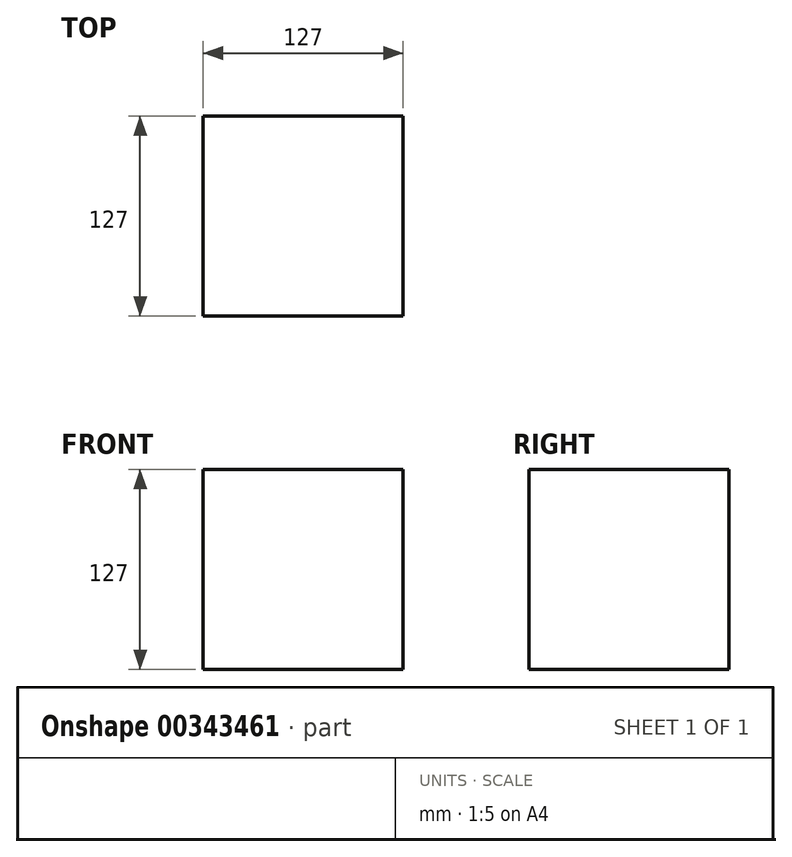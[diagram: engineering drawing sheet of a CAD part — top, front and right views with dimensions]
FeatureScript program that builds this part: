
annotation { "Feature Type Name" : "Feature", "Feature Type Description" : "" }
export const myFeature = defineFeature(function(context is Context, id is Id, definition is map)
    precondition{}
    {
        {
            var Q0;
            Q0=qCreatedBy(makeId("Front.planeOp"),FACE);
            var sketch = newSketch(context, id + "F0", { "sketchPlane" : qUnion([Q0])});
            skLineSegment(sketch, "E0.bottom", {"start": v(-90.88, 157.92) * mm, "end": v(36.12, 157.92) * mm});
            skLineSegment(sketch, "E0.top", {"start": v(-90.88, 30.92) * mm, "end": v(36.12, 30.92) * mm});
            skLineSegment(sketch, "E0.left", {"start": v(-90.88, 157.92) * mm, "end": v(-90.88, 30.92) * mm});
            skLineSegment(sketch, "E0.right", {"start": v(36.12, 157.92) * mm, "end": v(36.12, 30.92) * mm});
            skSolve(sketch);
        }
        {
            var Q0;
            Q0=makeQuery(id+"F0.imprint","IMPRINT",FACE,{"disambiguationData":[TD([[makeQuery(id+"F0.imprint","IMPRINT",EDGE,{"derivedFrom":sQuery(id+"F0.wireOp",EDGE,"E0.bottom")}),-1.0]])]});
            extrude(context, id + "F1", {"entities" : qUnion([Q0]), "depth" : 127 * mm});
        }
    });
